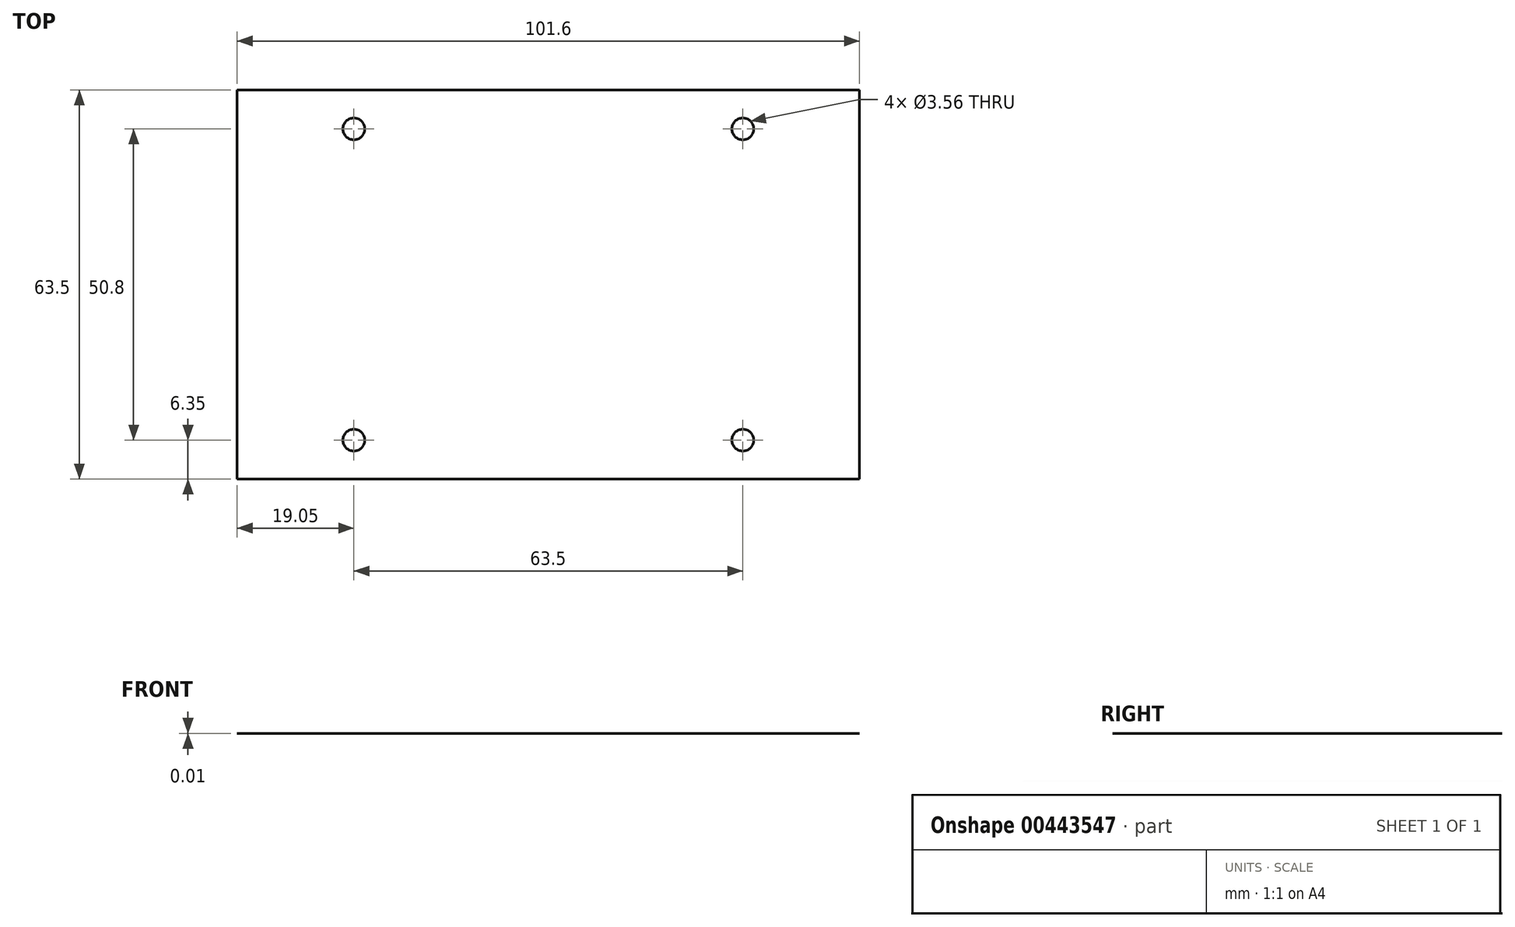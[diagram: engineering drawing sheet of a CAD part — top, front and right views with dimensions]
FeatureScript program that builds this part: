
annotation { "Feature Type Name" : "Feature", "Feature Type Description" : "" }
export const myFeature = defineFeature(function(context is Context, id is Id, definition is map)
    precondition{}
    {
        {
            var Q0;
            Q0=qCreatedBy(makeId("Top.planeOp"),FACE);
            var sketch = newSketch(context, id + "F0", { "sketchPlane" : qUnion([Q0])});
            skLineSegment(sketch, "E0.bottom", {"start": v(0, 0) * mm, "end": v(101.6, 0) * mm});
            skLineSegment(sketch, "E0.top", {"start": v(0, 63.5) * mm, "end": v(101.6, 63.5) * mm});
            skLineSegment(sketch, "E0.left", {"start": v(0, 0) * mm, "end": v(0, 63.5) * mm});
            skLineSegment(sketch, "E0.right", {"start": v(101.6, 0) * mm, "end": v(101.6, 63.5) * mm});
            skCircle(sketch, "E1", {"center": v(19.05, 6.35) * mm, "radius": 1.78 * mm});
            skCircle(sketch, "E2", {"center": v(82.55, 6.35) * mm, "radius": 1.78 * mm});
            skLineSegment(sketch, "E3", {"start": v(0, 31.75) * mm, "end": v(101.6, 31.75) * mm, "construction": true});
            skCircle(sketch, "E4.MirrorC", {"center": v(82.55, 57.15) * mm, "radius": 1.78 * mm});
            skCircle(sketch, "E5.MirrorC", {"center": v(19.05, 57.15) * mm, "radius": 1.78 * mm});
            skSolve(sketch);
        }
        {
            var Q0;
            Q0=makeQuery(id+"F0.imprint","IMPRINT",FACE,{"disambiguationData":[TD([[makeQuery(id+"F0.imprint","IMPRINT",EDGE,{"derivedFrom":sQuery(id+"F0.wireOp",EDGE,"E0.bottom")}),1.0]])]});
            extrude(context, id + "F1", {"entities" : qUnion([Q0]), "depth" : 1 / 101.6 * mm});
        }
    });
